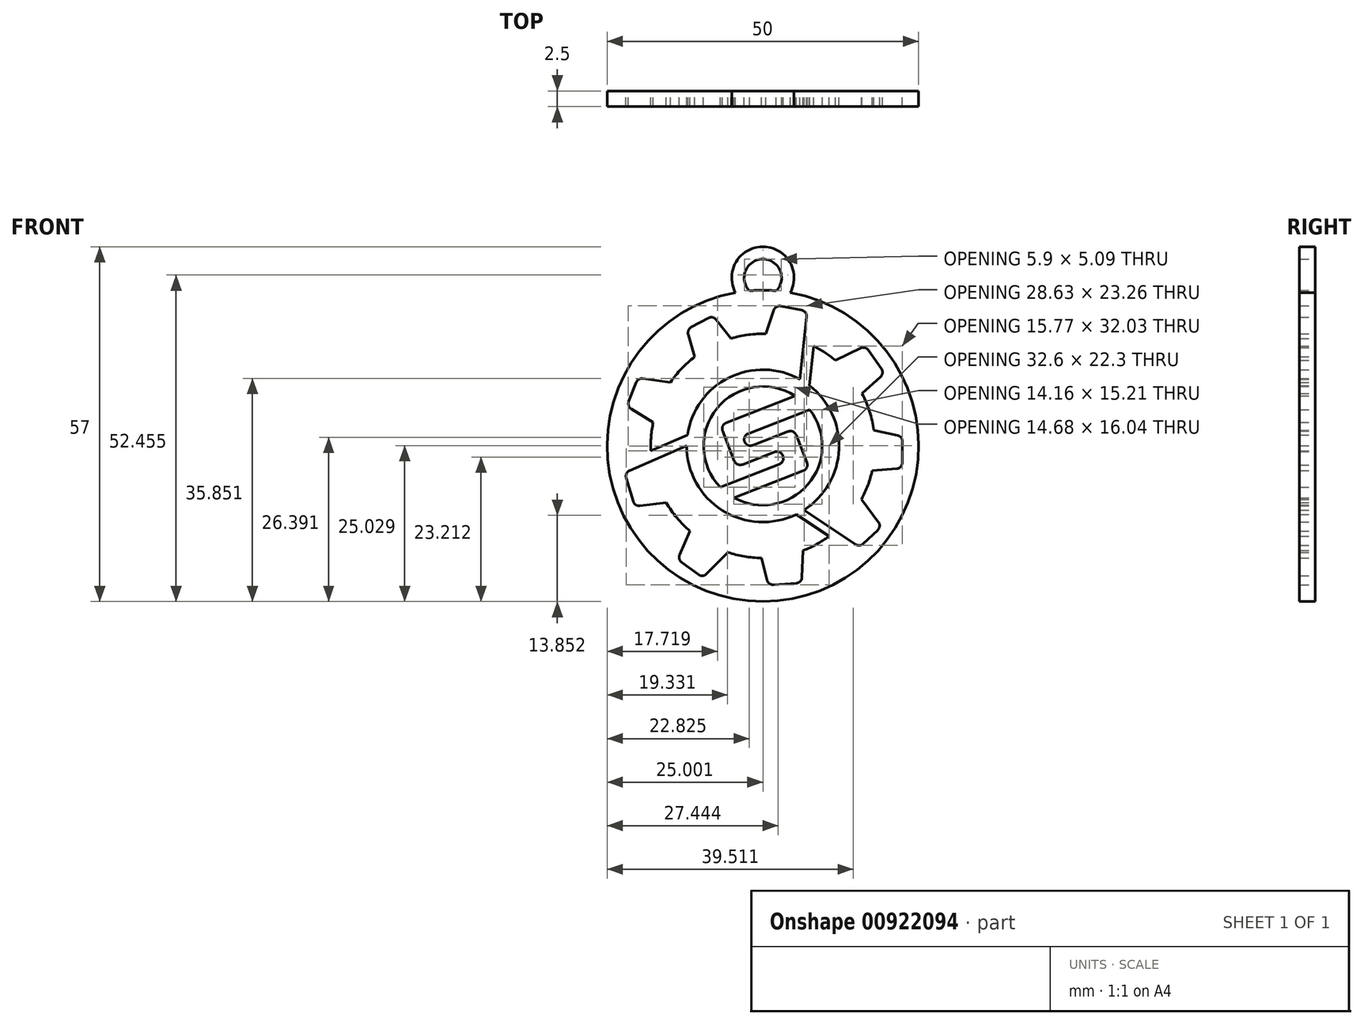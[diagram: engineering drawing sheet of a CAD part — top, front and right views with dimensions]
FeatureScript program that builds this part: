
annotation { "Feature Type Name" : "Feature", "Feature Type Description" : "" }
export const myFeature = defineFeature(function(context is Context, id is Id, definition is map)
    precondition{}
    {
        {
            var Q0;
            Q0=qCreatedBy(makeId("Front.planeOp"),FACE);
            var sketch = newSketch(context, id + "F0", { "sketchPlane" : qUnion([Q0])});
            skLineSegment(sketch, "E0", {"start": v(-59.04, 30.26) * mm, "end": v(-9.04, 30.26) * mm, "construction": true});
            skCircle(sketch, "E1", {"center": v(-34.04, 30.26) * mm, "radius": 9.53 * mm});
            skLineSegment(sketch, "E2", {"start": v(-40.88, 23.63) * mm, "end": v(-31.38, 27.32) * mm});
            skLineSegment(sketch, "E3", {"start": v(-30.81, 28.62) * mm, "end": v(-30.85, 28.72) * mm});
            skLineSegment(sketch, "E4", {"start": v(-32.15, 29.3) * mm, "end": v(-37.33, 27.27) * mm});
            skLineSegment(sketch, "E5", {"start": v(-38.63, 27.84) * mm, "end": v(-40.5, 32.67) * mm});
            skLineSegment(sketch, "E6", {"start": v(-39.94, 33.96) * mm, "end": v(-28.87, 38.27) * mm});
            skLineSegment(sketch, "E7", {"start": v(-26.5, 36.08) * mm, "end": v(-36.4, 32.22) * mm});
            skLineSegment(sketch, "E8", {"start": v(-36.97, 30.93) * mm, "end": v(-36.97, 30.92) * mm});
            skLineSegment(sketch, "E9", {"start": v(-35.68, 30.35) * mm, "end": v(-29.98, 32.57) * mm});
            skLineSegment(sketch, "E10", {"start": v(-28.68, 32) * mm, "end": v(-26.96, 27.57) * mm});
            skLineSegment(sketch, "E11", {"start": v(-27.53, 26.27) * mm, "end": v(-38.68, 21.94) * mm});
            skCircle(sketch, "E12", {"center": v(-34.04, 30.26) * mm, "radius": 12.24 * mm});
            skCircle(sketch, "E13", {"center": v(-34.04, 30.26) * mm, "radius": 18 * mm});
            skLineSegment(sketch, "E14", {"start": v(-28.09, 40.95) * mm, "end": v(-27.01, 50.98) * mm});
            skLineSegment(sketch, "E15", {"start": v(-27.81, 52.06) * mm, "end": v(-31.13, 52.72) * mm});
            skLineSegment(sketch, "E16", {"start": v(-32.27, 52.06) * mm, "end": v(-33.53, 48.26) * mm});
            skLineSegment(sketch, "E17", {"start": v(-39.13, 47.53) * mm, "end": v(-41.54, 50.54) * mm});
            skLineSegment(sketch, "E18", {"start": v(-42.8, 50.8) * mm, "end": v(-45.54, 49.32) * mm});
            skLineSegment(sketch, "E19", {"start": v(-46.02, 48.16) * mm, "end": v(-44.98, 44.56) * mm});
            skLineSegment(sketch, "E20", {"start": v(-48.87, 40.46) * mm, "end": v(-53.33, 41.08) * mm});
            skLineSegment(sketch, "E21", {"start": v(-54.4, 40.44) * mm, "end": v(-55.57, 37.38) * mm});
            skLineSegment(sketch, "E22", {"start": v(-55.15, 36.17) * mm, "end": v(-51.64, 34.04) * mm});
            skLineSegment(sketch, "E23", {"start": v(-46.28, 30.26) * mm, "end": v(-55.4, 26.31) * mm});
            skLineSegment(sketch, "E24", {"start": v(-55.97, 25.11) * mm, "end": v(-54.86, 21.35) * mm});
            skLineSegment(sketch, "E25", {"start": v(-53.78, 20.64) * mm, "end": v(-49.56, 21.13) * mm});
            skLineSegment(sketch, "E26", {"start": v(-45.75, 16.59) * mm, "end": v(-47.4, 12.76) * mm});
            skLineSegment(sketch, "E27", {"start": v(-47.08, 11.56) * mm, "end": v(-44.37, 9.58) * mm});
            skLineSegment(sketch, "E28", {"start": v(-43.07, 9.69) * mm, "end": v(-39.68, 13.16) * mm});
            skLineSegment(sketch, "E29", {"start": v(-34.28, 12.26) * mm, "end": v(-33.38, 8.72) * mm});
            skLineSegment(sketch, "E30", {"start": v(-32.35, 7.96) * mm, "end": v(-28.69, 8.2) * mm});
            skLineSegment(sketch, "E31", {"start": v(-27.75, 9.16) * mm, "end": v(-27.58, 13.46) * mm});
            skLineSegment(sketch, "E32", {"start": v(-27.41, 19.97) * mm, "end": v(-19.16, 14.44) * mm});
            skLineSegment(sketch, "E33", {"start": v(-17.91, 14.54) * mm, "end": v(-15.6, 16.73) * mm});
            skLineSegment(sketch, "E34", {"start": v(-15.5, 18.06) * mm, "end": v(-18.21, 21.68) * mm});
            skLineSegment(sketch, "E35", {"start": v(-16.48, 26.29) * mm, "end": v(-12.57, 26.59) * mm});
            skLineSegment(sketch, "E36", {"start": v(-11.64, 27.58) * mm, "end": v(-11.64, 30.98) * mm});
            skLineSegment(sketch, "E37", {"start": v(-12.43, 31.96) * mm, "end": v(-16.21, 32.76) * mm});
            skLineSegment(sketch, "E38", {"start": v(-18.12, 38.67) * mm, "end": v(-15.16, 41.35) * mm});
            skLineSegment(sketch, "E39", {"start": v(-15.01, 42.66) * mm, "end": v(-17.1, 45.64) * mm});
            skLineSegment(sketch, "E40", {"start": v(-18.35, 45.97) * mm, "end": v(-22.41, 44) * mm});
            skLineSegment(sketch, "E41", {"start": v(-52.02, 29.48) * mm, "end": v(-46.15, 32.02) * mm});
            skLineSegment(sketch, "E42", {"start": v(-26.56, 39.95) * mm, "end": v(-25.87, 46.3) * mm});
            skLineSegment(sketch, "E43", {"start": v(-28.67, 19.26) * mm, "end": v(-23.4, 15.73) * mm});
            skPoint(sketch, "E44.visualSharp", {"position": v(-55.87, 36.6) * mm});
            skArc(sketch, "E44.filletArc", {"start": v(-55.57, 37.38) * mm, "mid": v(-55.58, 36.7) * mm, "end": v(-55.15, 36.17) * mm});
            skPoint(sketch, "E45.visualSharp", {"position": v(-54.11, 41.19) * mm});
            skArc(sketch, "E45.filletArc", {"start": v(-53.33, 41.08) * mm, "mid": v(-53.97, 40.95) * mm, "end": v(-54.4, 40.44) * mm});
            skPoint(sketch, "E46.visualSharp", {"position": v(-46.25, 48.93) * mm});
            skArc(sketch, "E46.filletArc", {"start": v(-45.54, 49.32) * mm, "mid": v(-45.99, 48.82) * mm, "end": v(-46.02, 48.16) * mm});
            skPoint(sketch, "E47.visualSharp", {"position": v(-42.06, 51.2) * mm});
            skArc(sketch, "E47.filletArc", {"start": v(-41.54, 50.54) * mm, "mid": v(-42.13, 50.9) * mm, "end": v(-42.8, 50.8) * mm});
            skPoint(sketch, "E48.visualSharp", {"position": v(-32, 52.9) * mm});
            skArc(sketch, "E48.filletArc", {"start": v(-31.13, 52.72) * mm, "mid": v(-31.83, 52.6) * mm, "end": v(-32.27, 52.06) * mm});
            skPoint(sketch, "E49.visualSharp", {"position": v(-26.91, 51.89) * mm});
            skArc(sketch, "E49.filletArc", {"start": v(-27.01, 50.98) * mm, "mid": v(-27.2, 51.68) * mm, "end": v(-27.81, 52.06) * mm});
            skPoint(sketch, "E50.visualSharp", {"position": v(-17.58, 46.34) * mm});
            skArc(sketch, "E50.filletArc", {"start": v(-17.1, 45.64) * mm, "mid": v(-17.66, 46.03) * mm, "end": v(-18.35, 45.97) * mm});
            skPoint(sketch, "E51.visualSharp", {"position": v(-14.5, 41.94) * mm});
            skArc(sketch, "E51.filletArc", {"start": v(-15.16, 41.35) * mm, "mid": v(-14.84, 41.98) * mm, "end": v(-15.01, 42.66) * mm});
            skPoint(sketch, "E52.visualSharp", {"position": v(-11.64, 31.79) * mm});
            skArc(sketch, "E52.filletArc", {"start": v(-11.64, 30.98) * mm, "mid": v(-11.87, 31.6) * mm, "end": v(-12.43, 31.96) * mm});
            skPoint(sketch, "E53.visualSharp", {"position": v(-11.64, 26.66) * mm});
            skArc(sketch, "E53.filletArc", {"start": v(-12.57, 26.59) * mm, "mid": v(-11.91, 26.9) * mm, "end": v(-11.64, 27.58) * mm});
            skPoint(sketch, "E54.visualSharp", {"position": v(-14.97, 17.35) * mm});
            skArc(sketch, "E54.filletArc", {"start": v(-15.6, 16.73) * mm, "mid": v(-15.3, 17.37) * mm, "end": v(-15.5, 18.06) * mm});
            skPoint(sketch, "E55.visualSharp", {"position": v(-18.5, 14) * mm});
            skArc(sketch, "E55.filletArc", {"start": v(-19.16, 14.44) * mm, "mid": v(-18.51, 14.27) * mm, "end": v(-17.91, 14.54) * mm});
            skPoint(sketch, "E56.visualSharp", {"position": v(-27.8, 8.26) * mm});
            skArc(sketch, "E56.filletArc", {"start": v(-28.69, 8.2) * mm, "mid": v(-28.04, 8.5) * mm, "end": v(-27.75, 9.16) * mm});
            skPoint(sketch, "E57.visualSharp", {"position": v(-33.18, 7.91) * mm});
            skArc(sketch, "E57.filletArc", {"start": v(-33.38, 8.72) * mm, "mid": v(-33, 8.15) * mm, "end": v(-32.35, 7.96) * mm});
            skPoint(sketch, "E58.visualSharp", {"position": v(-43.67, 9.07) * mm});
            skArc(sketch, "E58.filletArc", {"start": v(-44.37, 9.58) * mm, "mid": v(-43.7, 9.4) * mm, "end": v(-43.07, 9.69) * mm});
            skPoint(sketch, "E59.visualSharp", {"position": v(-47.73, 12.03) * mm});
            skArc(sketch, "E59.filletArc", {"start": v(-47.4, 12.76) * mm, "mid": v(-47.46, 12.1) * mm, "end": v(-47.08, 11.56) * mm});
            skPoint(sketch, "E60.visualSharp", {"position": v(-54.62, 20.54) * mm});
            skArc(sketch, "E60.filletArc", {"start": v(-54.86, 21.35) * mm, "mid": v(-54.45, 20.8) * mm, "end": v(-53.78, 20.64) * mm});
            skPoint(sketch, "E61.visualSharp", {"position": v(-56.22, 25.96) * mm});
            skArc(sketch, "E61.filletArc", {"start": v(-55.4, 26.31) * mm, "mid": v(-55.92, 25.82) * mm, "end": v(-55.97, 25.11) * mm});
            skPoint(sketch, "E62.visualSharp", {"position": v(-40.87, 33.6) * mm});
            skArc(sketch, "E62.filletArc", {"start": v(-39.94, 33.96) * mm, "mid": v(-40.49, 33.43) * mm, "end": v(-40.5, 32.67) * mm});
            skPoint(sketch, "E63.visualSharp", {"position": v(-37.34, 31.86) * mm});
            skArc(sketch, "E63.filletArc", {"start": v(-36.4, 32.22) * mm, "mid": v(-36.96, 31.7) * mm, "end": v(-36.97, 30.93) * mm});
            skPoint(sketch, "E64.visualSharp", {"position": v(-36.61, 30) * mm});
            skArc(sketch, "E64.filletArc", {"start": v(-36.97, 30.92) * mm, "mid": v(-36.44, 30.37) * mm, "end": v(-35.68, 30.35) * mm});
            skPoint(sketch, "E65.visualSharp", {"position": v(-31.22, 29.65) * mm});
            skArc(sketch, "E65.filletArc", {"start": v(-30.85, 28.72) * mm, "mid": v(-31.38, 29.27) * mm, "end": v(-32.15, 29.3) * mm});
            skPoint(sketch, "E66.visualSharp", {"position": v(-30.45, 27.69) * mm});
            skArc(sketch, "E66.filletArc", {"start": v(-31.38, 27.32) * mm, "mid": v(-30.83, 27.85) * mm, "end": v(-30.81, 28.62) * mm});
            skPoint(sketch, "E67.visualSharp", {"position": v(-29.05, 32.93) * mm});
            skArc(sketch, "E67.filletArc", {"start": v(-28.68, 32) * mm, "mid": v(-29.21, 32.55) * mm, "end": v(-29.98, 32.57) * mm});
            skPoint(sketch, "E68.visualSharp", {"position": v(-38.27, 26.91) * mm});
            skArc(sketch, "E68.filletArc", {"start": v(-38.63, 27.84) * mm, "mid": v(-38.1, 27.3) * mm, "end": v(-37.33, 27.27) * mm});
            skPoint(sketch, "E69.visualSharp", {"position": v(-26.6, 26.64) * mm});
            skArc(sketch, "E69.filletArc", {"start": v(-27.53, 26.27) * mm, "mid": v(-26.98, 26.8) * mm, "end": v(-26.96, 27.57) * mm});
            skCircle(sketch, "E70", {"center": v(-34.04, 30.26) * mm, "radius": 25 * mm});
            skLineSegment(sketch, "E71", {"start": v(-34.04, 30.26) * mm, "end": v(-34.04, 55.26) * mm, "construction": true});
            skLineSegment(sketch, "E72", {"start": v(-34.04, 55.26) * mm, "end": v(-34.04, 57.26) * mm, "construction": true});
            skArc(sketch, "E73", {"start": v(-29.65, 54.87) * mm, "mid": v(-34.04, 62.26) * mm, "end": v(-38.43, 54.87) * mm});
            skArc(sketch, "E74", {"start": v(-31.89, 55.17) * mm, "mid": v(-34.04, 60.26) * mm, "end": v(-36.19, 55.17) * mm});
            skSolve(sketch);
        }
        {
            var Q0;
            Q0 = qSketchRegion(id + "F0", true);
            var Q1;
            {var subQ0=sQuery(id+"F0.wireOp",EDGE,"E1");var subQ7=makeQuery(id+"F0.imprint","INTERSECT",VERTEX,{"derivedFrom":[subQ0,sQuery(id+"F0.wireOp",EDGE,"E6")]});Q1=makeQuery(id+"F0.imprint","IMPRINT",FACE,{"disambiguationData":[TD([[makeQuery(id+"F0.imprint","IMPRINT",EDGE,{"disambiguationData":[TD([[subQ7,1.0]])],"derivedFrom":subQ0}),-1.0]])]});}
            var Q2;
            {var subQ3=sQuery(id+"F0.wireOp",EDGE,"E41");Q2=makeQuery(id+"F0.imprint","IMPRINT",FACE,{"disambiguationData":[TD([[makeQuery(id+"F0.imprint","IMPRINT",EDGE,{"derivedFrom":subQ3}),-1.0]])]});}
            var Q3;
            {var subQ3=sQuery(id+"F0.wireOp",EDGE,"E43");Q3=makeQuery(id+"F0.imprint","IMPRINT",FACE,{"disambiguationData":[TD([[makeQuery(id+"F0.imprint","IMPRINT",EDGE,{"derivedFrom":subQ3}),1.0]])]});}
            var Q4;
            {var subQ3=sQuery(id+"F0.wireOp",EDGE,"E42");Q4=makeQuery(id+"F0.imprint","IMPRINT",FACE,{"disambiguationData":[TD([[makeQuery(id+"F0.imprint","IMPRINT",EDGE,{"derivedFrom":subQ3}),1.0]])]});}
            var Q5;
            {var subQ3=sQuery(id+"F0.wireOp",EDGE,"E2");Q5=makeQuery(id+"F0.imprint","IMPRINT",FACE,{"disambiguationData":[TD([[makeQuery(id+"F0.imprint","IMPRINT",EDGE,{"derivedFrom":subQ3}),-1.0]])]});}
            extrude(context, id + "F1", {"entities" : qUnion([Q0, Q1, Q2, Q3, Q4, Q5]), "depth" : 2.5 * mm, "offsetDistance" : 25 * mm});
        }
    });
